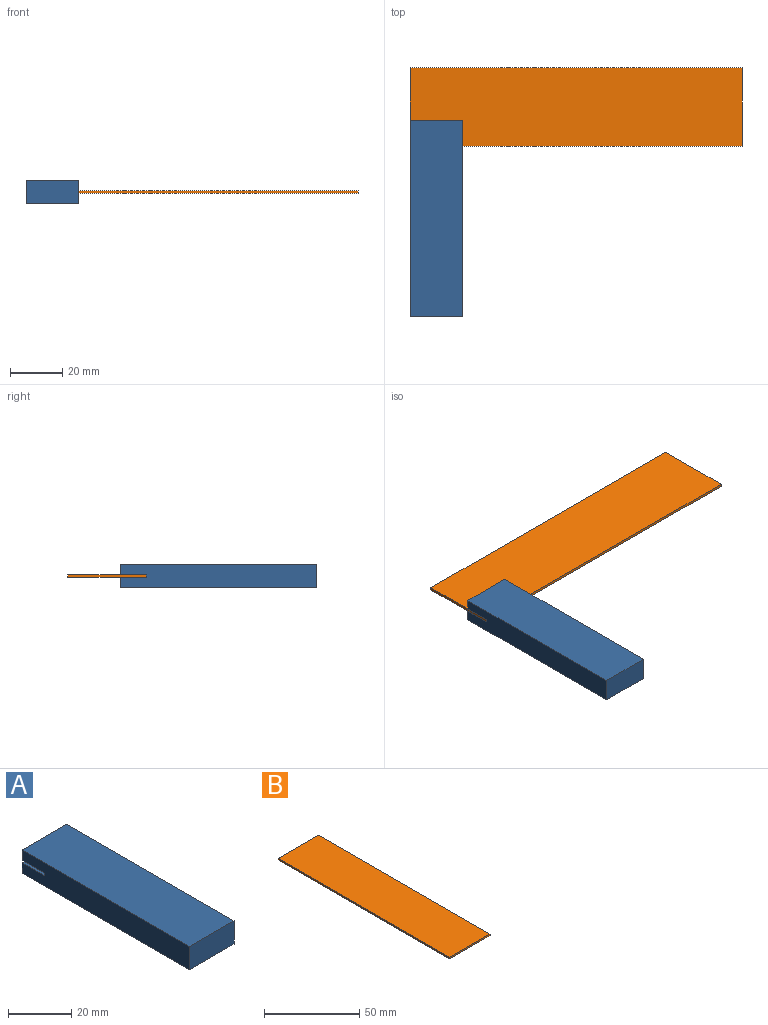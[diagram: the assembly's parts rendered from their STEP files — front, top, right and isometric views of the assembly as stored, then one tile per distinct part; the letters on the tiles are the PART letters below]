
ASSEMBLY  parts=2 mates=1
PART A: 10 faces, bbox 20x75x9 mm
  f0: plane 75x9mm, normal (-1,0,0), area 665mm2, adj f1,f2,f4,f5,f6,f7,f8,f9
  f1: plane 20x4mm, normal (0,1,0), area 80mm2, adj f0,f3,f6,f9
  f2: plane 20x9mm, normal (0,-1,0), area 180mm2, adj f0,f3,f5,f6
  f3: plane 75x9mm, normal (1,0,0), area 665mm2, adj f1,f2,f4,f5,f6,f7,f8,f9
  f4: plane 20x4mm, normal (0,1,0), area 80mm2, adj f0,f3,f5,f8
  f5: plane 75x20mm, normal (0,0,1), area 1500mm2, adj f0,f2,f3,f4
  f6: plane 75x20mm, normal (0,0,-1), area 1500mm2, adj f0,f1,f2,f3
  f7: plane 20x1mm, normal (0,1,0), area 20mm2, adj f0,f3,f8,f9
  f8: plane 20x10mm, normal (0,0,-1), area 200mm2, adj f0,f3,f4,f7
  f9: plane 20x10mm, normal (0,0,1), area 200mm2, adj f0,f1,f3,f7
PART B: 6 faces, bbox 30x127x1 mm
  f0: plane 127x1mm, normal (-1,0,0), area 127mm2, adj f1,f3,f4,f5
  f1: plane 30x1mm, normal (0,-1,0), area 30mm2, adj f0,f2,f4,f5
  f2: plane 127x1mm, normal (1,0,0), area 127mm2, adj f1,f3,f4,f5
  f3: plane 30x1mm, normal (0,1,0), area 30mm2, adj f0,f2,f4,f5
  f4: plane 127x30mm, normal (0,0,1), area 3810mm2, adj f0,f1,f2,f3
  f5: plane 127x30mm, normal (0,0,-1), area 3810mm2, adj f0,f1,f2,f3
PLACE A t=(-27.36,-37.67,48.94)mm
PLACE B rot(axis=(0,0,1),90deg) t=(99.64,27.33,52.94)mm
MATE fastened B.f4 <-> A.f8  axis (0,0,1) through (-27.36,27.33,53.94)mm
